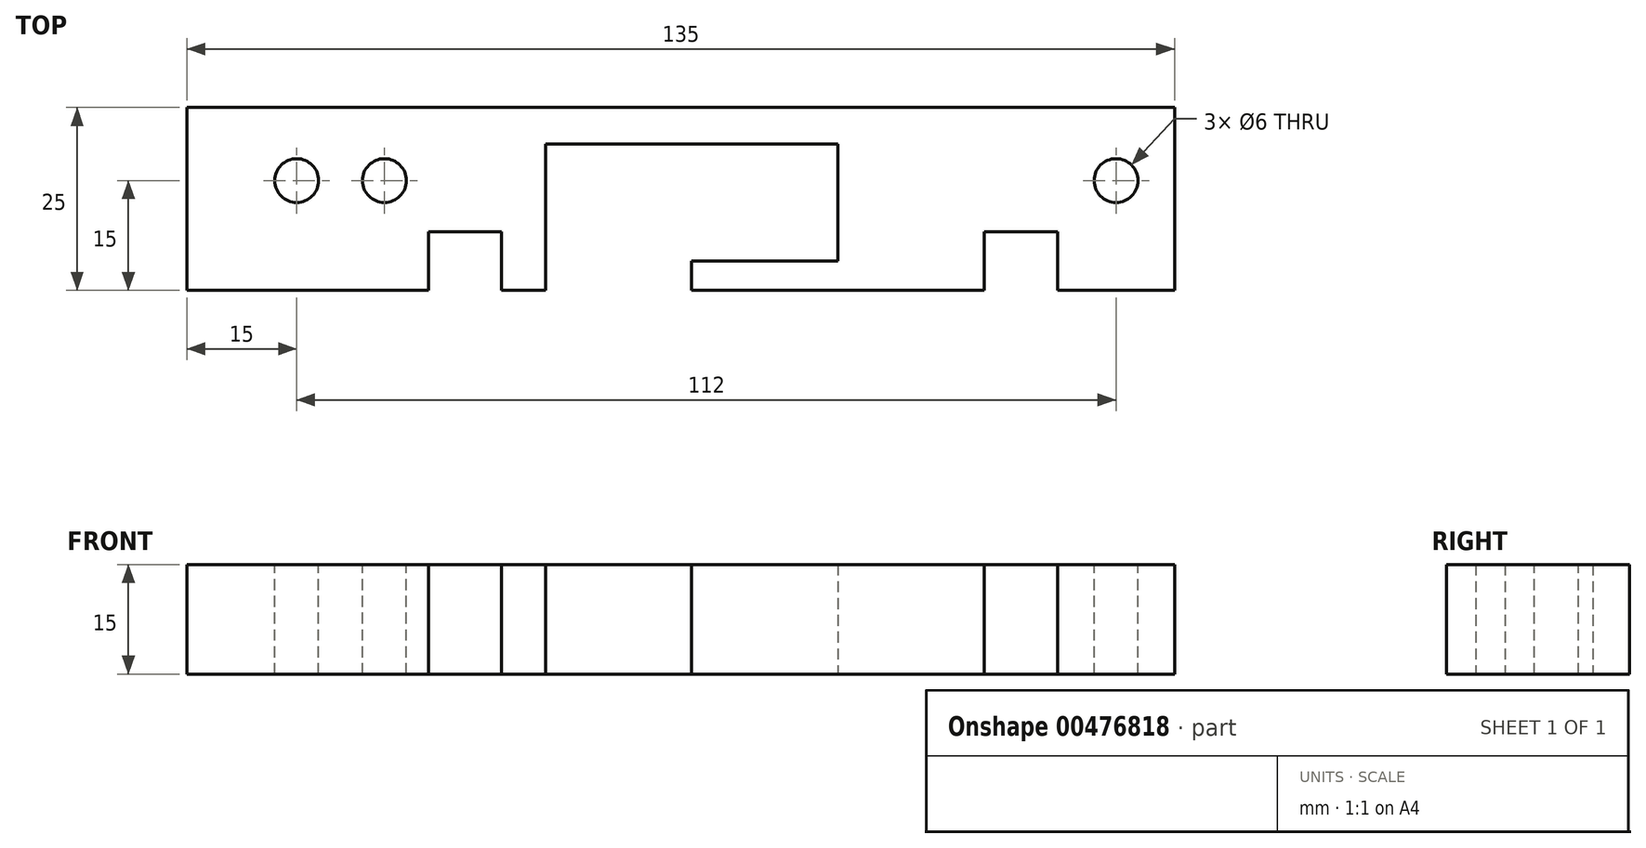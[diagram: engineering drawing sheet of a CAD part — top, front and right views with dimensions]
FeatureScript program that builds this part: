
annotation { "Feature Type Name" : "Feature", "Feature Type Description" : "" }
export const myFeature = defineFeature(function(context is Context, id is Id, definition is map)
    precondition{}
    {
        {
            var Q0;
            Q0=qCreatedBy(makeId("Top.planeOp"),FACE);
            var sketch = newSketch(context, id + "F0", { "sketchPlane" : qUnion([Q0])});
            skLineSegment(sketch, "E0.top", {"start": v(67.5, 12.5) * mm, "end": v(-67.5, 12.5) * mm});
            skLineSegment(sketch, "E0.left", {"start": v(67.5, -12.5) * mm, "end": v(67.5, 12.5) * mm});
            skLineSegment(sketch, "E0.right", {"start": v(-67.5, -12.5) * mm, "end": v(-67.5, 12.5) * mm});
            skPoint(sketch, "E0.middle", {"position": v(0, 0) * mm});
            skLineSegment(sketch, "E1.top", {"start": v(-34.5, -4.5) * mm, "end": v(-24.5, -4.5) * mm});
            skLineSegment(sketch, "E1.left", {"start": v(-34.5, -12.5) * mm, "end": v(-34.5, -4.5) * mm});
            skLineSegment(sketch, "E1.right", {"start": v(-24.5, -12.5) * mm, "end": v(-24.5, -4.5) * mm});
            skLineSegment(sketch, "E2.top", {"start": v(-18.5, 7.5) * mm, "end": v(21.5, 7.5) * mm});
            skLineSegment(sketch, "E2.left", {"start": v(-18.5, -12.5) * mm, "end": v(-18.5, 7.5) * mm});
            skLineSegment(sketch, "E3.top", {"start": v(41.5, -4.5) * mm, "end": v(51.5, -4.5) * mm});
            skLineSegment(sketch, "E3.left", {"start": v(41.5, -12.5) * mm, "end": v(41.5, -4.5) * mm});
            skLineSegment(sketch, "E3.right", {"start": v(51.5, -12.5) * mm, "end": v(51.5, -4.5) * mm});
            skLineSegment(sketch, "E4.top", {"start": v(21.5, -8.5) * mm, "end": v(1.5, -8.5) * mm});
            skLineSegment(sketch, "E4.right", {"start": v(1.5, -12.5) * mm, "end": v(1.5, -8.5) * mm});
            skLineSegment(sketch, "E5", {"start": v(-67.5, -12.5) * mm, "end": v(-34.5, -12.5) * mm});
            skLineSegment(sketch, "E6", {"start": v(-24.5, -12.5) * mm, "end": v(-18.5, -12.5) * mm});
            skLineSegment(sketch, "E7", {"start": v(67.5, -12.5) * mm, "end": v(51.5, -12.5) * mm});
            skLineSegment(sketch, "E8", {"start": v(21.5, 7.5) * mm, "end": v(21.5, -8.5) * mm});
            skLineSegment(sketch, "E9", {"start": v(41.5, -12.5) * mm, "end": v(1.5, -12.5) * mm});
            skSolve(sketch);
        }
        {
            var Q0;
            Q0=makeQuery(id+"F0.imprint","IMPRINT",FACE,{"disambiguationData":[TD([[makeQuery(id+"F0.imprint","IMPRINT",EDGE,{"derivedFrom":sQuery(id+"F0.wireOp",EDGE,"E0.top")}),1.0]])]});
            extrude(context, id + "F1", {"entities" : qUnion([Q0]), "depth" : 15 * mm});
        }
        {
            var Q0;
            Q0=makeQuery(id+"F1.opExtrude","CAP_FACE",FACE,{"disambiguationData":[OSD([sQuery(id+"F0.wireOp",EDGE,"E0.top"),sQuery(id+"F0.wireOp",EDGE,"E0.left"),sQuery(id+"F0.wireOp",EDGE,"E0.right"),sQuery(id+"F0.wireOp",EDGE,"E1.top"),sQuery(id+"F0.wireOp",EDGE,"E1.left"),sQuery(id+"F0.wireOp",EDGE,"E1.right"),sQuery(id+"F0.wireOp",EDGE,"E2.top"),sQuery(id+"F0.wireOp",EDGE,"E2.left"),sQuery(id+"F0.wireOp",EDGE,"E3.top"),sQuery(id+"F0.wireOp",EDGE,"E3.left"),sQuery(id+"F0.wireOp",EDGE,"E3.right"),sQuery(id+"F0.wireOp",EDGE,"E4.top"),sQuery(id+"F0.wireOp",EDGE,"E4.right"),sQuery(id+"F0.wireOp",EDGE,"E5"),sQuery(id+"F0.wireOp",EDGE,"E6"),sQuery(id+"F0.wireOp",EDGE,"E7"),sQuery(id+"F0.wireOp",EDGE,"E8"),sQuery(id+"F0.wireOp",EDGE,"E9")])],"isStart":false});
            var sketch = newSketch(context, id + "F2", { "sketchPlane" : qUnion([Q0])});
            skCircle(sketch, "E10", {"center": v(-52.5, 2.5) * mm, "radius": 3 * mm});
            skCircle(sketch, "E11", {"center": v(-40.5, 2.5) * mm, "radius": 3 * mm});
            skCircle(sketch, "E12", {"center": v(59.5, 2.5) * mm, "radius": 3 * mm});
            skSolve(sketch);
        }
        {
            var Q0;
            Q0=sQuery(id+"F2.wireOp",VERTEX,"E10.center");
            var Q1;
            Q1=sQuery(id+"F2.wireOp",VERTEX,"E11.center");
            var Q2;
            Q2=sQuery(id+"F2.wireOp",VERTEX,"E12.center");
            var Q3;
            Q3=makeQuery(id+"F1.opExtrude","SWEPT_BODY",BODY,{"disambiguationData":[OSD([sQuery(id+"F0.wireOp",EDGE,"E0.top"),sQuery(id+"F0.wireOp",EDGE,"E0.left"),sQuery(id+"F0.wireOp",EDGE,"E0.right"),sQuery(id+"F0.wireOp",EDGE,"E1.top"),sQuery(id+"F0.wireOp",EDGE,"E1.left"),sQuery(id+"F0.wireOp",EDGE,"E1.right"),sQuery(id+"F0.wireOp",EDGE,"E2.top"),sQuery(id+"F0.wireOp",EDGE,"E2.left"),sQuery(id+"F0.wireOp",EDGE,"E3.top"),sQuery(id+"F0.wireOp",EDGE,"E3.left"),sQuery(id+"F0.wireOp",EDGE,"E3.right"),sQuery(id+"F0.wireOp",EDGE,"E4.top"),sQuery(id+"F0.wireOp",EDGE,"E4.right"),sQuery(id+"F0.wireOp",EDGE,"E5"),sQuery(id+"F0.wireOp",EDGE,"E6"),sQuery(id+"F0.wireOp",EDGE,"E7"),sQuery(id+"F0.wireOp",EDGE,"E8"),sQuery(id+"F0.wireOp",EDGE,"E9")])]});
            hole(context, id + "F3", {"style" : HoleStyle.SIMPLE, "endStyle" : HoleEndStyle.THROUGH, "holeDiameter" : 6 * mm, "isTappedThrough" : true, "tappedDepth" : 12 * mm, "tapClearance" : 3, "locations" : qUnion([Q0, Q1, Q2]), "scope" : qUnion([Q3])});
        }
    });
